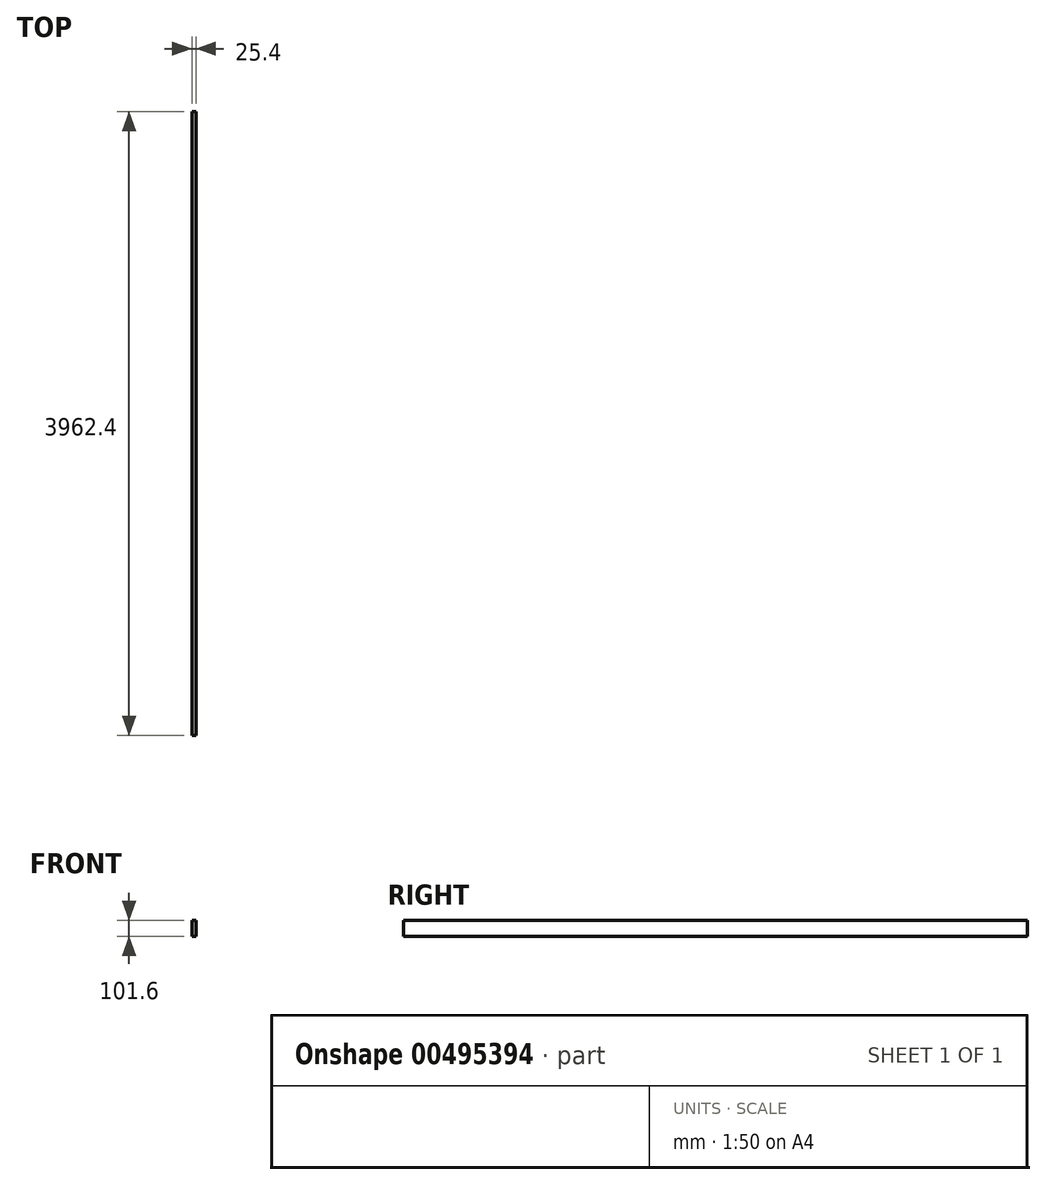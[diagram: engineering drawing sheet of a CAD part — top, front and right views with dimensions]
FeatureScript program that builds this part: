
annotation { "Feature Type Name" : "Feature", "Feature Type Description" : "" }
export const myFeature = defineFeature(function(context is Context, id is Id, definition is map)
    precondition{}
    {
        {
            var Q0;
            Q0=qCreatedBy(makeId("Front.planeOp"),FACE);
            var sketch = newSketch(context, id + "F0", { "sketchPlane" : qUnion([Q0])});
            skLineSegment(sketch, "E0.bottom", {"start": v(0, 0) * mm, "end": v(25.4, 0) * mm});
            skLineSegment(sketch, "E0.top", {"start": v(0, 101.6) * mm, "end": v(25.4, 101.6) * mm});
            skLineSegment(sketch, "E0.left", {"start": v(0, 0) * mm, "end": v(0, 101.6) * mm});
            skLineSegment(sketch, "E0.right", {"start": v(25.4, 0) * mm, "end": v(25.4, 101.6) * mm});
            skSolve(sketch);
        }
        {
            var Q0;
            Q0 = qSketchRegion(id + "F0", true);
            extrude(context, id + "F1", {"entities" : qUnion([Q0]), "depth" : 3962.4 * mm, "offsetDistance" : 25.4 * mm});
        }
    });
